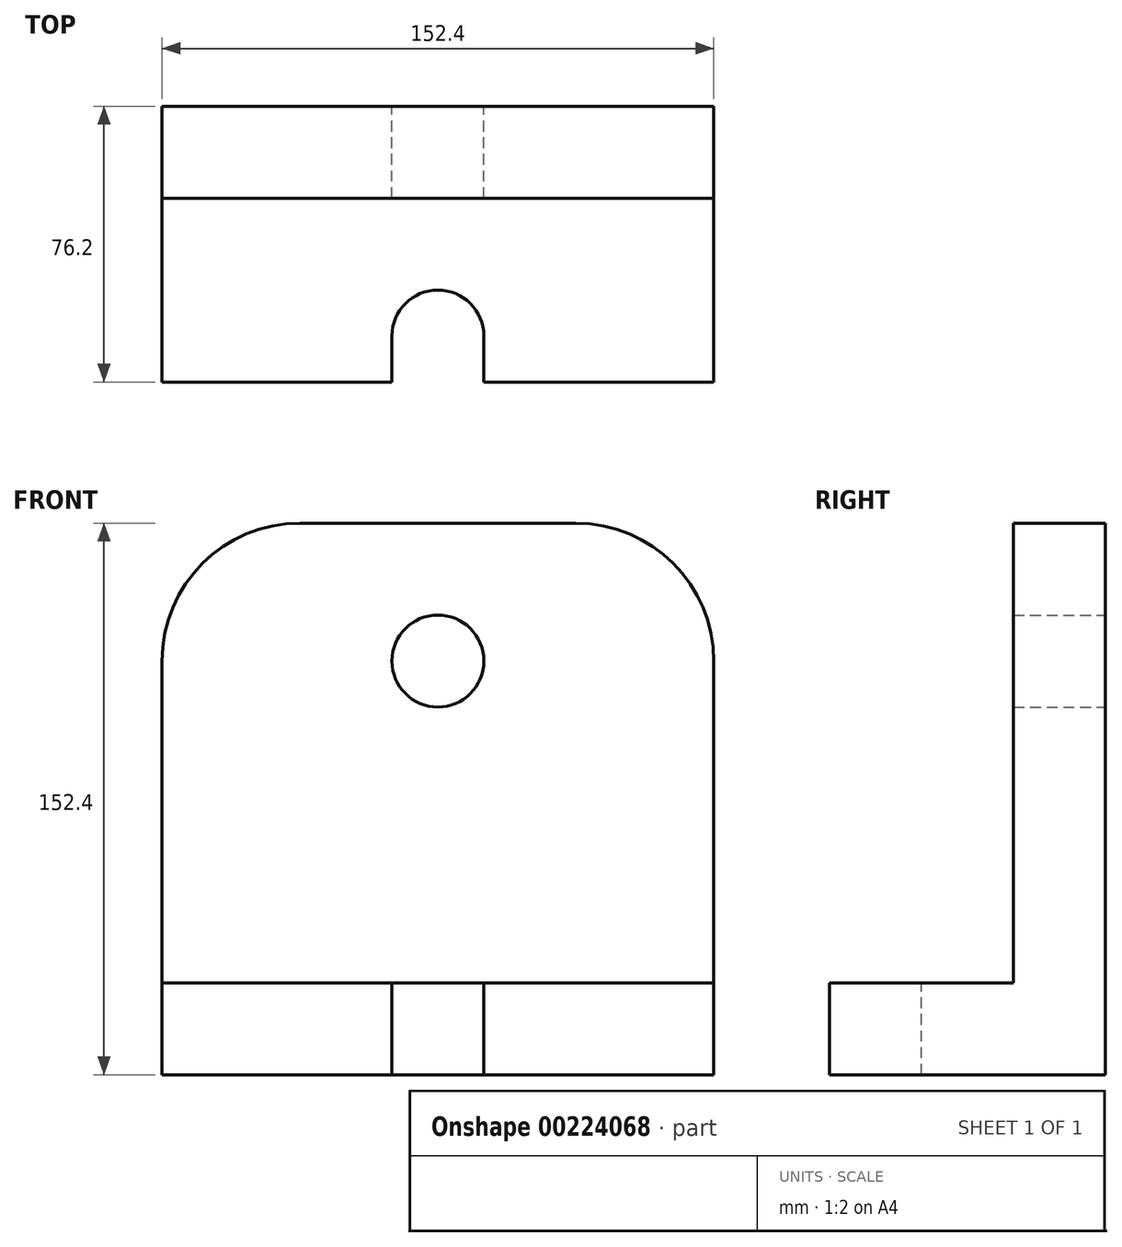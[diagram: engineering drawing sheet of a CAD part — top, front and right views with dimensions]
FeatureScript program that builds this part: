
annotation { "Feature Type Name" : "Feature", "Feature Type Description" : "" }
export const myFeature = defineFeature(function(context is Context, id is Id, definition is map)
    precondition{}
    {
        {
            var Q0;
            Q0=qCreatedBy(makeId("Right.planeOp"),FACE);
            var sketch = newSketch(context, id + "F0", { "sketchPlane" : qUnion([Q0])});
            skLineSegment(sketch, "E0", {"start": v(0, 0) * mm, "end": v(0, 152.4) * mm});
            skLineSegment(sketch, "E1", {"start": v(0, 0) * mm, "end": v(-76.2, 0) * mm});
            skLineSegment(sketch, "E2", {"start": v(-76.2, 0) * mm, "end": v(-76.2, 25.4) * mm});
            skLineSegment(sketch, "E3", {"start": v(0, 152.4) * mm, "end": v(-25.4, 152.4) * mm});
            skLineSegment(sketch, "E4", {"start": v(-25.4, 152.4) * mm, "end": v(-25.4, 25.4) * mm});
            skLineSegment(sketch, "E5", {"start": v(-76.2, 25.4) * mm, "end": v(-25.4, 25.4) * mm});
            skSolve(sketch);
        }
        {
            var Q0;
            Q0=makeQuery(id+"F0.imprint","IMPRINT",FACE,{"disambiguationData":[TD([[makeQuery(id+"F0.imprint","IMPRINT",EDGE,{"derivedFrom":sQuery(id+"F0.wireOp",EDGE,"E0")}),1.0]])]});
            extrude(context, id + "F1", {"entities" : qUnion([Q0]), "endBound" : BoundingType.SYMMETRIC, "depth" : 152.4 * mm});
        }
        {
            var Q0;
            Q0=makeQuery(id+"F1.opExtrude","SWEPT_FACE",FACE,{"disambiguationData":[OSD([sQuery(id+"F0.wireOp",EDGE,"E0")])]});
            var sketch = newSketch(context, id + "F2", { "sketchPlane" : qUnion([Q0])});
            skLineSegment(sketch, "E6", {"start": v(0, 152.4) * mm, "end": v(0, 114.3) * mm});
            skPoint(sketch, "E6.endSnap0", {"position": v(0, 152.4) * mm});
            skCircle(sketch, "E7", {"center": v(0, 114.3) * mm, "radius": 12.7 * mm});
            skSolve(sketch);
        }
        {
            var Q0;
            Q0 = qSketchRegion(id + "F2", true);
            extrude(context, id + "F3", {"entities" : qUnion([Q0]), "operationType" : NewBodyOperationType.REMOVE, "oppositeDirection" : true, "depth" : 25.4 * mm});
        }
        {
            var Q0;
            Q0=makeQuery(id+"F1.opExtrude","SWEPT_FACE",FACE,{"disambiguationData":[OSD([sQuery(id+"F0.wireOp",EDGE,"E5")])]});
            var sketch = newSketch(context, id + "F4", { "sketchPlane" : qUnion([Q0])});
            skPoint(sketch, "E8.endSnap0", {"position": v(0, -76.2) * mm});
            skLineSegment(sketch, "E9", {"start": v(12.7, -63.5) * mm, "end": v(12.7, -76.2) * mm});
            skLineSegment(sketch, "E10", {"start": v(-12.7, -63.5) * mm, "end": v(-12.7, -76.2) * mm});
            skArc(sketch, "E11", {"start": v(-12.7, -63.5) * mm, "mid": v(0, -50.8) * mm, "end": v(12.7, -63.5) * mm});
            skLineSegment(sketch, "E12", {"start": v(-12.7, -76.2) * mm, "end": v(12.7, -76.2) * mm});
            skSolve(sketch);
        }
        {
            var Q0;
            Q0=makeQuery(id+"F4.imprint","IMPRINT",FACE,{"disambiguationData":[TD([[makeQuery(id+"F4.imprint","IMPRINT",EDGE,{"derivedFrom":sQuery(id+"F4.wireOp",EDGE,"E9")}),-1.0]])]});
            extrude(context, id + "F5", {"entities" : qUnion([Q0]), "operationType" : NewBodyOperationType.REMOVE, "oppositeDirection" : true, "depth" : 45.47 * mm});
        }
        {
            var Q0;
            Q0=makeQuery(id+"F1.opExtrude","CAP_EDGE",EDGE,{"disambiguationData":[OSD([sQuery(id+"F0.wireOp",EDGE,"E3")])],"isStart":false});
            fillet(context, id + "F6", {"entities" : qUnion([Q0]), "radius" : 38.1 * mm, "tangentPropagation" : true, "allowEdgeOverflow" : false});
        }
        {
            var Q0;
            Q0=makeQuery(id+"F1.opExtrude","CAP_EDGE",EDGE,{"disambiguationData":[OSD([sQuery(id+"F0.wireOp",EDGE,"E3")])],"isStart":true});
            fillet(context, id + "F7", {"entities" : qUnion([Q0]), "radius" : 38.1 * mm, "tangentPropagation" : true, "allowEdgeOverflow" : false});
        }
    });
